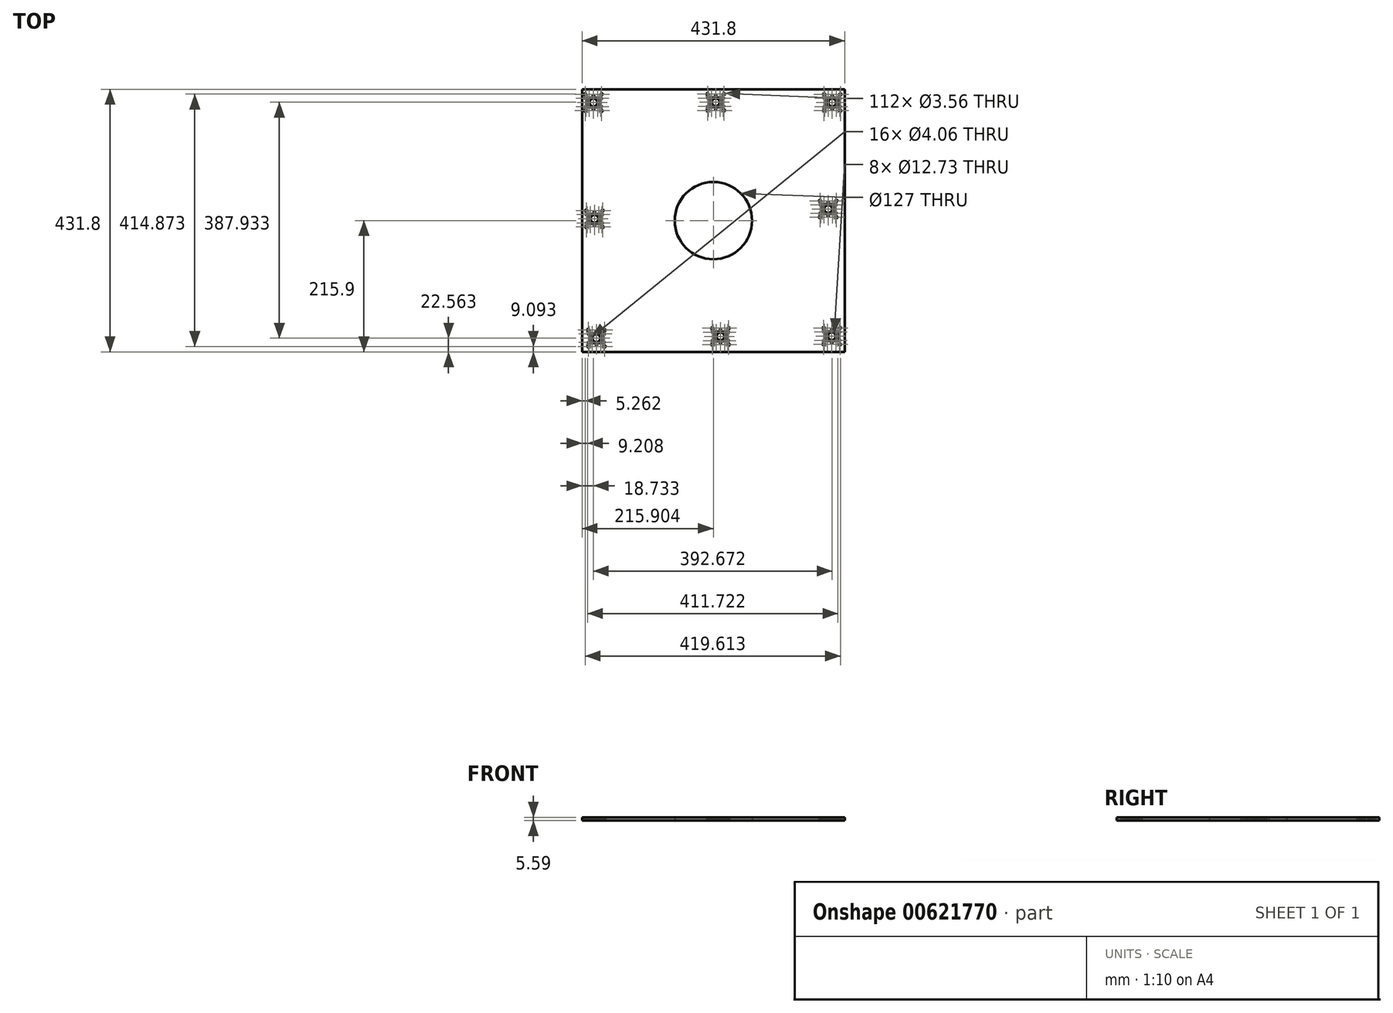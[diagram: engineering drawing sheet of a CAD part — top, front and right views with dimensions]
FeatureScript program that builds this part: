
annotation { "Feature Type Name" : "Feature", "Feature Type Description" : "" }
export const myFeature = defineFeature(function(context is Context, id is Id, definition is map)
    precondition{}
    {
        {
            var Q0;
            Q0=qCreatedBy(makeId("Top.planeOp"),FACE);
            var sketch = newSketch(context, id + "F0", { "sketchPlane" : qUnion([Q0])});
            skLineSegment(sketch, "E0.bottom", {"start": v(148.17, 142.22) * mm, "end": v(-283.63, 142.22) * mm});
            skLineSegment(sketch, "E0.top", {"start": v(148.17, -289.58) * mm, "end": v(-283.63, -289.58) * mm});
            skLineSegment(sketch, "E0.left", {"start": v(148.17, 142.22) * mm, "end": v(148.17, -289.58) * mm});
            skLineSegment(sketch, "E0.right", {"start": v(-283.63, 142.22) * mm, "end": v(-283.63, -289.58) * mm});
            skPoint(sketch, "E0.middle", {"position": v(-67.73, -73.68) * mm});
            skCircle(sketch, "E1", {"center": v(-264.9, 130.29) * mm, "radius": 1.78 * mm});
            skPoint(sketch, "E1.first.point", {"position": v(-264.85, 132.07) * mm});
            skPoint(sketch, "E1.second.point", {"position": v(-264.68, 128.52) * mm});
            skPoint(sketch, "E1.third.point", {"position": v(-266.67, 130.25) * mm});
            skCircle(sketch, "E2", {"center": v(-264.9, 110.73) * mm, "radius": 1.78 * mm});
            skPoint(sketch, "E2.first.point", {"position": v(-264.74, 108.96) * mm});
            skPoint(sketch, "E2.second.point", {"position": v(-263.7, 112.04) * mm});
            skPoint(sketch, "E2.third.point", {"position": v(-265.58, 112.37) * mm});
            skPoint(sketch, "E3.first.point", {"position": v(-271.06, 105.36) * mm});
            skPoint(sketch, "E3.second.point", {"position": v(-269.23, 108.3) * mm});
            skPoint(sketch, "E3.third.point", {"position": v(-272.02, 107.92) * mm});
            skPoint(sketch, "E4.first.point", {"position": v(-258.08, 105.76) * mm});
            skPoint(sketch, "E4.second.point", {"position": v(-259.26, 108.82) * mm});
            skPoint(sketch, "E4.third.point", {"position": v(-260.86, 106.16) * mm});
            skPoint(sketch, "E5.first.point", {"position": v(-259.07, 132.22) * mm});
            skPoint(sketch, "E5.second.point", {"position": v(-259.1, 135.74) * mm});
            skPoint(sketch, "E5.third.point", {"position": v(-261.06, 133.62) * mm});
            skPoint(sketch, "E6.first.point", {"position": v(-272.16, 133.4) * mm});
            skPoint(sketch, "E6.second.point", {"position": v(-269.17, 135.18) * mm});
            skPoint(sketch, "E6.third.point", {"position": v(-271.36, 135.52) * mm});
            skCircle(sketch, "E7", {"center": v(-278.37, 133.98) * mm, "radius": 1.78 * mm});
            skPoint(sketch, "E7.first.point", {"position": v(-278.3, 135.76) * mm});
            skPoint(sketch, "E7.second.point", {"position": v(-277.44, 132.47) * mm});
            skPoint(sketch, "E7.third.point", {"position": v(-279.88, 133.05) * mm});
            skCircle(sketch, "E8", {"center": v(-251.43, 133.98) * mm, "radius": 1.78 * mm});
            skPoint(sketch, "E8.first.point", {"position": v(-250.93, 132.27) * mm});
            skPoint(sketch, "E8.second.point", {"position": v(-251.22, 135.75) * mm});
            skPoint(sketch, "E8.third.point", {"position": v(-253.2, 133.75) * mm});
            skCircle(sketch, "E9", {"center": v(-252.76, 127.42) * mm, "radius": 1.78 * mm});
            skPoint(sketch, "E9.first.point", {"position": v(-252.48, 129.18) * mm});
            skPoint(sketch, "E9.second.point", {"position": v(-252.73, 125.65) * mm});
            skPoint(sketch, "E9.third.point", {"position": v(-253.73, 128.91) * mm});
            skCircle(sketch, "E10", {"center": v(-257.98, 127.42) * mm, "radius": 1.78 * mm});
            skPoint(sketch, "E10.first.point", {"position": v(-257.5, 125.71) * mm});
            skPoint(sketch, "E10.second.point", {"position": v(-257.84, 129.2) * mm});
            skPoint(sketch, "E10.third.point", {"position": v(-259.28, 128.64) * mm});
            skCircle(sketch, "E11", {"center": v(-271.81, 127.42) * mm, "radius": 1.78 * mm});
            skPoint(sketch, "E11.first.point", {"position": v(-272.14, 125.68) * mm});
            skPoint(sketch, "E11.second.point", {"position": v(-270.14, 128.03) * mm});
            skPoint(sketch, "E11.third.point", {"position": v(-272.1, 129.18) * mm});
            skCircle(sketch, "E12", {"center": v(-277.03, 127.42) * mm, "radius": 1.78 * mm});
            skPoint(sketch, "E12.first.point", {"position": v(-277, 125.65) * mm});
            skPoint(sketch, "E12.second.point", {"position": v(-276.26, 129.03) * mm});
            skPoint(sketch, "E12.third.point", {"position": v(-276.91, 129.2) * mm});
            skCircle(sketch, "E13", {"center": v(-274.42, 120.5) * mm, "radius": 2.03 * mm});
            skPoint(sketch, "E13.first.point", {"position": v(-273.06, 122.02) * mm});
            skPoint(sketch, "E13.second.point", {"position": v(-272.94, 119.12) * mm});
            skPoint(sketch, "E13.third.point", {"position": v(-276.18, 121.53) * mm});
            skCircle(sketch, "E14", {"center": v(-264.9, 120.5) * mm, "radius": 6.36 * mm});
            skPoint(sketch, "E14.first.point", {"position": v(-266.11, 114.26) * mm});
            skPoint(sketch, "E14.second.point", {"position": v(-259.17, 123.3) * mm});
            skPoint(sketch, "E14.third.point", {"position": v(-268.92, 125.44) * mm});
            skCircle(sketch, "E15", {"center": v(-255.37, 120.5) * mm, "radius": 2.03 * mm});
            skPoint(sketch, "E15.first.point", {"position": v(-255.23, 118.48) * mm});
            skPoint(sketch, "E15.second.point", {"position": v(-253.75, 121.73) * mm});
            skPoint(sketch, "E15.third.point", {"position": v(-255.78, 122.5) * mm});
            skCircle(sketch, "E16", {"center": v(-252.76, 113.6) * mm, "radius": 1.78 * mm});
            skPoint(sketch, "E16.first.point", {"position": v(-252.64, 111.82) * mm});
            skPoint(sketch, "E16.second.point", {"position": v(-251.22, 114.48) * mm});
            skPoint(sketch, "E16.third.point", {"position": v(-253.96, 114.91) * mm});
            skCircle(sketch, "E17", {"center": v(-257.98, 113.6) * mm, "radius": 1.78 * mm});
            skPoint(sketch, "E17.first.point", {"position": v(-258.1, 111.82) * mm});
            skPoint(sketch, "E17.second.point", {"position": v(-257.07, 115.12) * mm});
            skPoint(sketch, "E17.third.point", {"position": v(-258.86, 115.14) * mm});
            skCircle(sketch, "E18", {"center": v(-251.43, 107.04) * mm, "radius": 1.78 * mm});
            skPoint(sketch, "E18.first.point", {"position": v(-252.64, 105.74) * mm});
            skPoint(sketch, "E18.second.point", {"position": v(-250.38, 108.48) * mm});
            skPoint(sketch, "E18.third.point", {"position": v(-250.31, 105.65) * mm});
            skCircle(sketch, "E19", {"center": v(-278.37, 107.04) * mm, "radius": 1.78 * mm});
            skPoint(sketch, "E19.first.point", {"position": v(-278.95, 105.36) * mm});
            skPoint(sketch, "E19.second.point", {"position": v(-276.98, 108.16) * mm});
            skPoint(sketch, "E19.third.point", {"position": v(-279.64, 108.28) * mm});
            skCircle(sketch, "E20", {"center": v(-277.03, 113.6) * mm, "radius": 1.78 * mm});
            skPoint(sketch, "E20.first.point", {"position": v(-277.43, 111.86) * mm});
            skPoint(sketch, "E20.second.point", {"position": v(-275.8, 114.88) * mm});
            skPoint(sketch, "E20.third.point", {"position": v(-277.51, 115.3) * mm});
            skCircle(sketch, "E21", {"center": v(-271.81, 113.6) * mm, "radius": 1.78 * mm});
            skPoint(sketch, "E21.first.point", {"position": v(-272.24, 111.87) * mm});
            skPoint(sketch, "E21.second.point", {"position": v(-271.06, 115.2) * mm});
            skPoint(sketch, "E21.third.point", {"position": v(-272.97, 114.94) * mm});
            skCircle(sketch, "E22", {"center": v(127.77, 130.29) * mm, "radius": 1.78 * mm});
            skPoint(sketch, "E22.first.point", {"position": v(127.83, 132.07) * mm});
            skPoint(sketch, "E22.second.point", {"position": v(128, 128.52) * mm});
            skPoint(sketch, "E22.third.point", {"position": v(126, 130.25) * mm});
            skCircle(sketch, "E23", {"center": v(127.77, 110.73) * mm, "radius": 1.78 * mm});
            skPoint(sketch, "E23.first.point", {"position": v(127.93, 108.96) * mm});
            skPoint(sketch, "E23.second.point", {"position": v(128.98, 112.04) * mm});
            skPoint(sketch, "E23.third.point", {"position": v(127.1, 112.37) * mm});
            skPoint(sketch, "E24.first.point", {"position": v(121.62, 105.36) * mm});
            skPoint(sketch, "E24.second.point", {"position": v(123.44, 108.3) * mm});
            skPoint(sketch, "E24.third.point", {"position": v(120.65, 107.92) * mm});
            skPoint(sketch, "E25.first.point", {"position": v(134.6, 105.76) * mm});
            skPoint(sketch, "E25.second.point", {"position": v(133.41, 108.82) * mm});
            skPoint(sketch, "E25.third.point", {"position": v(131.81, 106.16) * mm});
            skPoint(sketch, "E26.first.point", {"position": v(133.6, 132.22) * mm});
            skPoint(sketch, "E26.second.point", {"position": v(133.57, 135.74) * mm});
            skPoint(sketch, "E26.third.point", {"position": v(131.61, 133.62) * mm});
            skPoint(sketch, "E27.first.point", {"position": v(120.51, 133.4) * mm});
            skPoint(sketch, "E27.second.point", {"position": v(123.5, 135.18) * mm});
            skPoint(sketch, "E27.third.point", {"position": v(121.31, 135.52) * mm});
            skCircle(sketch, "E28", {"center": v(114.3, 133.98) * mm, "radius": 1.78 * mm});
            skPoint(sketch, "E28.first.point", {"position": v(114.38, 135.76) * mm});
            skPoint(sketch, "E28.second.point", {"position": v(115.24, 132.47) * mm});
            skPoint(sketch, "E28.third.point", {"position": v(112.8, 133.05) * mm});
            skCircle(sketch, "E29", {"center": v(141.25, 133.98) * mm, "radius": 1.78 * mm});
            skPoint(sketch, "E29.first.point", {"position": v(141.74, 132.27) * mm});
            skPoint(sketch, "E29.second.point", {"position": v(141.45, 135.75) * mm});
            skPoint(sketch, "E29.third.point", {"position": v(139.48, 133.75) * mm});
            skCircle(sketch, "E30", {"center": v(139.91, 127.42) * mm, "radius": 1.78 * mm});
            skPoint(sketch, "E30.first.point", {"position": v(140.2, 129.18) * mm});
            skPoint(sketch, "E30.second.point", {"position": v(139.94, 125.65) * mm});
            skPoint(sketch, "E30.third.point", {"position": v(138.94, 128.91) * mm});
            skCircle(sketch, "E31", {"center": v(134.69, 127.42) * mm, "radius": 1.78 * mm});
            skPoint(sketch, "E31.first.point", {"position": v(135.18, 125.71) * mm});
            skPoint(sketch, "E31.second.point", {"position": v(134.83, 129.2) * mm});
            skPoint(sketch, "E31.third.point", {"position": v(133.4, 128.64) * mm});
            skCircle(sketch, "E32", {"center": v(120.86, 127.42) * mm, "radius": 1.78 * mm});
            skPoint(sketch, "E32.first.point", {"position": v(120.54, 125.68) * mm});
            skPoint(sketch, "E32.second.point", {"position": v(122.53, 128.03) * mm});
            skPoint(sketch, "E32.third.point", {"position": v(120.58, 129.18) * mm});
            skCircle(sketch, "E33", {"center": v(115.64, 127.42) * mm, "radius": 1.78 * mm});
            skPoint(sketch, "E33.first.point", {"position": v(115.67, 125.65) * mm});
            skPoint(sketch, "E33.second.point", {"position": v(116.41, 129.03) * mm});
            skPoint(sketch, "E33.third.point", {"position": v(115.76, 129.2) * mm});
            skCircle(sketch, "E34", {"center": v(118.25, 120.5) * mm, "radius": 2.03 * mm});
            skPoint(sketch, "E34.first.point", {"position": v(119.61, 122.02) * mm});
            skPoint(sketch, "E34.second.point", {"position": v(119.74, 119.12) * mm});
            skPoint(sketch, "E34.third.point", {"position": v(116.5, 121.53) * mm});
            skCircle(sketch, "E35", {"center": v(127.77, 120.5) * mm, "radius": 6.36 * mm});
            skPoint(sketch, "E35.first.point", {"position": v(126.56, 114.26) * mm});
            skPoint(sketch, "E35.second.point", {"position": v(133.5, 123.3) * mm});
            skPoint(sketch, "E35.third.point", {"position": v(123.75, 125.44) * mm});
            skCircle(sketch, "E36", {"center": v(137.3, 120.5) * mm, "radius": 2.03 * mm});
            skPoint(sketch, "E36.first.point", {"position": v(137.44, 118.48) * mm});
            skPoint(sketch, "E36.second.point", {"position": v(138.93, 121.73) * mm});
            skPoint(sketch, "E36.third.point", {"position": v(136.9, 122.5) * mm});
            skCircle(sketch, "E37", {"center": v(139.91, 113.6) * mm, "radius": 1.78 * mm});
            skPoint(sketch, "E37.first.point", {"position": v(140.03, 111.82) * mm});
            skPoint(sketch, "E37.second.point", {"position": v(141.45, 114.48) * mm});
            skPoint(sketch, "E37.third.point", {"position": v(138.72, 114.91) * mm});
            skCircle(sketch, "E38", {"center": v(134.69, 113.6) * mm, "radius": 1.78 * mm});
            skPoint(sketch, "E38.first.point", {"position": v(134.58, 111.82) * mm});
            skPoint(sketch, "E38.second.point", {"position": v(135.6, 115.12) * mm});
            skPoint(sketch, "E38.third.point", {"position": v(133.81, 115.14) * mm});
            skCircle(sketch, "E39", {"center": v(141.25, 107.04) * mm, "radius": 1.78 * mm});
            skPoint(sketch, "E39.first.point", {"position": v(140.03, 105.74) * mm});
            skPoint(sketch, "E39.second.point", {"position": v(142.3, 108.48) * mm});
            skPoint(sketch, "E39.third.point", {"position": v(142.36, 105.65) * mm});
            skCircle(sketch, "E40", {"center": v(114.3, 107.04) * mm, "radius": 1.78 * mm});
            skPoint(sketch, "E40.first.point", {"position": v(113.73, 105.36) * mm});
            skPoint(sketch, "E40.second.point", {"position": v(115.69, 108.16) * mm});
            skPoint(sketch, "E40.third.point", {"position": v(113.03, 108.28) * mm});
            skCircle(sketch, "E41", {"center": v(115.64, 113.6) * mm, "radius": 1.78 * mm});
            skPoint(sketch, "E41.first.point", {"position": v(115.24, 111.86) * mm});
            skPoint(sketch, "E41.second.point", {"position": v(116.87, 114.88) * mm});
            skPoint(sketch, "E41.third.point", {"position": v(115.16, 115.3) * mm});
            skCircle(sketch, "E42", {"center": v(120.86, 113.6) * mm, "radius": 1.78 * mm});
            skPoint(sketch, "E42.first.point", {"position": v(120.43, 111.87) * mm});
            skPoint(sketch, "E42.second.point", {"position": v(121.62, 115.2) * mm});
            skPoint(sketch, "E42.third.point", {"position": v(119.7, 114.94) * mm});
            skCircle(sketch, "E43", {"center": v(-63.84, 130.7) * mm, "radius": 1.78 * mm});
            skPoint(sketch, "E43.first.point", {"position": v(-63.78, 132.47) * mm});
            skPoint(sketch, "E43.second.point", {"position": v(-63.62, 128.93) * mm});
            skPoint(sketch, "E43.third.point", {"position": v(-65.61, 130.66) * mm});
            skCircle(sketch, "E44", {"center": v(-63.84, 111.14) * mm, "radius": 1.78 * mm});
            skPoint(sketch, "E44.first.point", {"position": v(-63.68, 109.37) * mm});
            skPoint(sketch, "E44.second.point", {"position": v(-62.63, 112.44) * mm});
            skPoint(sketch, "E44.third.point", {"position": v(-64.52, 112.78) * mm});
            skPoint(sketch, "E45.first.point", {"position": v(-70, 105.76) * mm});
            skPoint(sketch, "E45.second.point", {"position": v(-68.17, 108.71) * mm});
            skPoint(sketch, "E45.third.point", {"position": v(-70.96, 108.32) * mm});
            skPoint(sketch, "E46.first.point", {"position": v(-57.02, 106.17) * mm});
            skPoint(sketch, "E46.second.point", {"position": v(-58.2, 109.22) * mm});
            skPoint(sketch, "E46.third.point", {"position": v(-59.8, 106.56) * mm});
            skPoint(sketch, "E47.first.point", {"position": v(-58, 132.63) * mm});
            skPoint(sketch, "E47.second.point", {"position": v(-58.04, 136.15) * mm});
            skPoint(sketch, "E47.third.point", {"position": v(-60, 134.03) * mm});
            skPoint(sketch, "E48.first.point", {"position": v(-71.1, 133.8) * mm});
            skPoint(sketch, "E48.second.point", {"position": v(-68.1, 135.6) * mm});
            skPoint(sketch, "E48.third.point", {"position": v(-70.3, 135.93) * mm});
            skCircle(sketch, "E49", {"center": v(-77.3, 134.39) * mm, "radius": 1.78 * mm});
            skPoint(sketch, "E49.first.point", {"position": v(-77.23, 136.16) * mm});
            skPoint(sketch, "E49.second.point", {"position": v(-76.38, 132.87) * mm});
            skPoint(sketch, "E49.third.point", {"position": v(-78.82, 133.45) * mm});
            skCircle(sketch, "E50", {"center": v(-50.37, 134.39) * mm, "radius": 1.78 * mm});
            skPoint(sketch, "E50.first.point", {"position": v(-49.87, 132.68) * mm});
            skPoint(sketch, "E50.second.point", {"position": v(-50.16, 136.15) * mm});
            skPoint(sketch, "E50.third.point", {"position": v(-52.13, 134.16) * mm});
            skCircle(sketch, "E51", {"center": v(-51.7, 127.83) * mm, "radius": 1.78 * mm});
            skPoint(sketch, "E51.first.point", {"position": v(-51.42, 129.59) * mm});
            skPoint(sketch, "E51.second.point", {"position": v(-51.67, 126.05) * mm});
            skPoint(sketch, "E51.third.point", {"position": v(-52.67, 129.32) * mm});
            skCircle(sketch, "E52", {"center": v(-56.92, 127.83) * mm, "radius": 1.78 * mm});
            skPoint(sketch, "E52.first.point", {"position": v(-56.43, 126.12) * mm});
            skPoint(sketch, "E52.second.point", {"position": v(-56.78, 129.6) * mm});
            skPoint(sketch, "E52.third.point", {"position": v(-58.21, 129.05) * mm});
            skCircle(sketch, "E53", {"center": v(-70.75, 127.83) * mm, "radius": 1.78 * mm});
            skPoint(sketch, "E53.first.point", {"position": v(-71.08, 126.08) * mm});
            skPoint(sketch, "E53.second.point", {"position": v(-69.08, 128.43) * mm});
            skPoint(sketch, "E53.third.point", {"position": v(-71.03, 129.59) * mm});
            skCircle(sketch, "E54", {"center": v(-75.97, 127.83) * mm, "radius": 1.78 * mm});
            skPoint(sketch, "E54.first.point", {"position": v(-75.94, 126.05) * mm});
            skPoint(sketch, "E54.second.point", {"position": v(-75.2, 129.43) * mm});
            skPoint(sketch, "E54.third.point", {"position": v(-75.85, 129.6) * mm});
            skCircle(sketch, "E55", {"center": v(-73.36, 120.92) * mm, "radius": 2.03 * mm});
            skPoint(sketch, "E55.first.point", {"position": v(-72, 122.43) * mm});
            skPoint(sketch, "E55.second.point", {"position": v(-71.88, 119.53) * mm});
            skPoint(sketch, "E55.third.point", {"position": v(-75.12, 121.94) * mm});
            skCircle(sketch, "E56", {"center": v(-63.84, 120.92) * mm, "radius": 6.36 * mm});
            skPoint(sketch, "E56.first.point", {"position": v(-65.05, 114.67) * mm});
            skPoint(sketch, "E56.second.point", {"position": v(-58.11, 123.7) * mm});
            skPoint(sketch, "E56.third.point", {"position": v(-67.86, 125.85) * mm});
            skCircle(sketch, "E57", {"center": v(-54.31, 120.92) * mm, "radius": 2.03 * mm});
            skPoint(sketch, "E57.first.point", {"position": v(-54.17, 118.89) * mm});
            skPoint(sketch, "E57.second.point", {"position": v(-52.69, 122.13) * mm});
            skPoint(sketch, "E57.third.point", {"position": v(-54.72, 122.9) * mm});
            skCircle(sketch, "E58", {"center": v(-51.7, 114) * mm, "radius": 1.78 * mm});
            skPoint(sketch, "E58.first.point", {"position": v(-51.58, 112.23) * mm});
            skPoint(sketch, "E58.second.point", {"position": v(-50.16, 114.88) * mm});
            skPoint(sketch, "E58.third.point", {"position": v(-52.9, 115.32) * mm});
            skCircle(sketch, "E59", {"center": v(-56.92, 114) * mm, "radius": 1.78 * mm});
            skPoint(sketch, "E59.first.point", {"position": v(-57.03, 112.23) * mm});
            skPoint(sketch, "E59.second.point", {"position": v(-56.01, 115.53) * mm});
            skPoint(sketch, "E59.third.point", {"position": v(-57.8, 115.55) * mm});
            skCircle(sketch, "E60", {"center": v(-50.37, 107.45) * mm, "radius": 1.78 * mm});
            skPoint(sketch, "E60.first.point", {"position": v(-51.58, 106.14) * mm});
            skPoint(sketch, "E60.second.point", {"position": v(-49.32, 108.88) * mm});
            skPoint(sketch, "E60.third.point", {"position": v(-49.25, 106.06) * mm});
            skCircle(sketch, "E61", {"center": v(-77.3, 107.45) * mm, "radius": 1.78 * mm});
            skPoint(sketch, "E61.first.point", {"position": v(-77.89, 105.76) * mm});
            skPoint(sketch, "E61.second.point", {"position": v(-75.92, 108.56) * mm});
            skPoint(sketch, "E61.third.point", {"position": v(-78.58, 108.68) * mm});
            skCircle(sketch, "E62", {"center": v(-75.97, 114) * mm, "radius": 1.78 * mm});
            skPoint(sketch, "E62.first.point", {"position": v(-76.37, 112.27) * mm});
            skPoint(sketch, "E62.second.point", {"position": v(-74.74, 115.29) * mm});
            skPoint(sketch, "E62.third.point", {"position": v(-76.45, 115.71) * mm});
            skCircle(sketch, "E63", {"center": v(-70.75, 114) * mm, "radius": 1.78 * mm});
            skPoint(sketch, "E63.first.point", {"position": v(-71.18, 112.27) * mm});
            skPoint(sketch, "E63.second.point", {"position": v(-70, 115.6) * mm});
            skPoint(sketch, "E63.third.point", {"position": v(-71.9, 115.35) * mm});
            skCircle(sketch, "E64", {"center": v(-263.17, -60.9) * mm, "radius": 1.78 * mm});
            skPoint(sketch, "E64.first.point", {"position": v(-263.11, -59.11) * mm});
            skPoint(sketch, "E64.second.point", {"position": v(-262.95, -62.66) * mm});
            skPoint(sketch, "E64.third.point", {"position": v(-264.94, -60.93) * mm});
            skCircle(sketch, "E65", {"center": v(-263.17, -80.45) * mm, "radius": 1.78 * mm});
            skPoint(sketch, "E65.first.point", {"position": v(-263, -82.22) * mm});
            skPoint(sketch, "E65.second.point", {"position": v(-261.96, -79.14) * mm});
            skPoint(sketch, "E65.third.point", {"position": v(-263.85, -78.8) * mm});
            skPoint(sketch, "E66.first.point", {"position": v(-269.33, -85.82) * mm});
            skPoint(sketch, "E66.second.point", {"position": v(-267.5, -82.87) * mm});
            skPoint(sketch, "E66.third.point", {"position": v(-270.3, -83.26) * mm});
            skPoint(sketch, "E67.first.point", {"position": v(-256.35, -85.42) * mm});
            skPoint(sketch, "E67.second.point", {"position": v(-257.53, -82.36) * mm});
            skPoint(sketch, "E67.third.point", {"position": v(-259.13, -85.02) * mm});
            skPoint(sketch, "E68.first.point", {"position": v(-257.34, -58.96) * mm});
            skPoint(sketch, "E68.second.point", {"position": v(-257.37, -55.44) * mm});
            skPoint(sketch, "E68.third.point", {"position": v(-259.33, -57.56) * mm});
            skPoint(sketch, "E69.first.point", {"position": v(-270.43, -57.78) * mm});
            skPoint(sketch, "E69.second.point", {"position": v(-267.44, -56) * mm});
            skPoint(sketch, "E69.third.point", {"position": v(-269.63, -55.66) * mm});
            skCircle(sketch, "E70", {"center": v(-276.64, -57.2) * mm, "radius": 1.78 * mm});
            skPoint(sketch, "E70.first.point", {"position": v(-276.56, -55.42) * mm});
            skPoint(sketch, "E70.second.point", {"position": v(-275.7, -58.71) * mm});
            skPoint(sketch, "E70.third.point", {"position": v(-278.15, -58.13) * mm});
            skCircle(sketch, "E71", {"center": v(-249.7, -57.2) * mm, "radius": 1.78 * mm});
            skPoint(sketch, "E71.first.point", {"position": v(-249.2, -58.9) * mm});
            skPoint(sketch, "E71.second.point", {"position": v(-249.5, -55.43) * mm});
            skPoint(sketch, "E71.third.point", {"position": v(-251.46, -57.43) * mm});
            skCircle(sketch, "E72", {"center": v(-251.03, -63.76) * mm, "radius": 1.78 * mm});
            skPoint(sketch, "E72.first.point", {"position": v(-250.75, -62) * mm});
            skPoint(sketch, "E72.second.point", {"position": v(-251, -65.53) * mm});
            skPoint(sketch, "E72.third.point", {"position": v(-252, -62.27) * mm});
            skCircle(sketch, "E73", {"center": v(-256.25, -63.76) * mm, "radius": 1.78 * mm});
            skPoint(sketch, "E73.first.point", {"position": v(-255.76, -65.47) * mm});
            skPoint(sketch, "E73.second.point", {"position": v(-256.11, -61.98) * mm});
            skPoint(sketch, "E73.third.point", {"position": v(-257.54, -62.53) * mm});
            skCircle(sketch, "E74", {"center": v(-270.08, -63.76) * mm, "radius": 1.78 * mm});
            skPoint(sketch, "E74.first.point", {"position": v(-270.4, -65.5) * mm});
            skPoint(sketch, "E74.second.point", {"position": v(-268.4, -63.15) * mm});
            skPoint(sketch, "E74.third.point", {"position": v(-270.36, -62) * mm});
            skCircle(sketch, "E75", {"center": v(-275.3, -63.76) * mm, "radius": 1.78 * mm});
            skPoint(sketch, "E75.first.point", {"position": v(-275.27, -65.53) * mm});
            skPoint(sketch, "E75.second.point", {"position": v(-274.53, -62.15) * mm});
            skPoint(sketch, "E75.third.point", {"position": v(-275.18, -61.98) * mm});
            skCircle(sketch, "E76", {"center": v(-272.7, -70.67) * mm, "radius": 2.03 * mm});
            skPoint(sketch, "E76.first.point", {"position": v(-271.33, -69.16) * mm});
            skPoint(sketch, "E76.second.point", {"position": v(-271.2, -72.06) * mm});
            skPoint(sketch, "E76.third.point", {"position": v(-274.45, -69.65) * mm});
            skCircle(sketch, "E77", {"center": v(-263.17, -70.67) * mm, "radius": 6.36 * mm});
            skPoint(sketch, "E77.first.point", {"position": v(-264.38, -76.92) * mm});
            skPoint(sketch, "E77.second.point", {"position": v(-257.44, -67.89) * mm});
            skPoint(sketch, "E77.third.point", {"position": v(-267.19, -65.74) * mm});
            skCircle(sketch, "E78", {"center": v(-253.64, -70.67) * mm, "radius": 2.03 * mm});
            skPoint(sketch, "E78.first.point", {"position": v(-253.5, -72.7) * mm});
            skPoint(sketch, "E78.second.point", {"position": v(-252.02, -69.45) * mm});
            skPoint(sketch, "E78.third.point", {"position": v(-254.05, -68.68) * mm});
            skCircle(sketch, "E79", {"center": v(-251.03, -77.58) * mm, "radius": 1.78 * mm});
            skPoint(sketch, "E79.first.point", {"position": v(-250.9, -79.36) * mm});
            skPoint(sketch, "E79.second.point", {"position": v(-249.49, -76.7) * mm});
            skPoint(sketch, "E79.third.point", {"position": v(-252.22, -76.27) * mm});
            skCircle(sketch, "E80", {"center": v(-256.25, -77.58) * mm, "radius": 1.78 * mm});
            skPoint(sketch, "E80.first.point", {"position": v(-256.36, -79.36) * mm});
            skPoint(sketch, "E80.second.point", {"position": v(-255.34, -76.06) * mm});
            skPoint(sketch, "E80.third.point", {"position": v(-257.13, -76.04) * mm});
            skCircle(sketch, "E81", {"center": v(-249.7, -84.14) * mm, "radius": 1.78 * mm});
            skPoint(sketch, "E81.first.point", {"position": v(-250.9, -85.44) * mm});
            skPoint(sketch, "E81.second.point", {"position": v(-248.65, -82.7) * mm});
            skPoint(sketch, "E81.third.point", {"position": v(-248.58, -85.53) * mm});
            skCircle(sketch, "E82", {"center": v(-276.64, -84.14) * mm, "radius": 1.78 * mm});
            skPoint(sketch, "E82.first.point", {"position": v(-277.22, -85.82) * mm});
            skPoint(sketch, "E82.second.point", {"position": v(-275.25, -83.02) * mm});
            skPoint(sketch, "E82.third.point", {"position": v(-277.91, -82.9) * mm});
            skCircle(sketch, "E83", {"center": v(-275.3, -77.58) * mm, "radius": 1.78 * mm});
            skPoint(sketch, "E83.first.point", {"position": v(-275.7, -79.32) * mm});
            skPoint(sketch, "E83.second.point", {"position": v(-274.07, -76.3) * mm});
            skPoint(sketch, "E83.third.point", {"position": v(-275.78, -75.87) * mm});
            skCircle(sketch, "E84", {"center": v(-270.08, -77.58) * mm, "radius": 1.78 * mm});
            skPoint(sketch, "E84.first.point", {"position": v(-270.5, -79.31) * mm});
            skPoint(sketch, "E84.second.point", {"position": v(-269.33, -75.98) * mm});
            skPoint(sketch, "E84.third.point", {"position": v(-271.24, -76.24) * mm});
            skCircle(sketch, "E85", {"center": v(-260.03, -257.24) * mm, "radius": 1.78 * mm});
            skPoint(sketch, "E85.first.point", {"position": v(-259.97, -255.46) * mm});
            skPoint(sketch, "E85.second.point", {"position": v(-259.8, -259) * mm});
            skPoint(sketch, "E85.third.point", {"position": v(-261.8, -257.28) * mm});
            skCircle(sketch, "E86", {"center": v(-260.03, -276.8) * mm, "radius": 1.78 * mm});
            skPoint(sketch, "E86.first.point", {"position": v(-259.87, -278.57) * mm});
            skPoint(sketch, "E86.second.point", {"position": v(-258.82, -275.49) * mm});
            skPoint(sketch, "E86.third.point", {"position": v(-260.7, -275.15) * mm});
            skPoint(sketch, "E87.first.point", {"position": v(-266.18, -282.17) * mm});
            skPoint(sketch, "E87.second.point", {"position": v(-264.36, -279.22) * mm});
            skPoint(sketch, "E87.third.point", {"position": v(-267.15, -279.6) * mm});
            skPoint(sketch, "E88.first.point", {"position": v(-253.2, -281.76) * mm});
            skPoint(sketch, "E88.second.point", {"position": v(-254.39, -278.71) * mm});
            skPoint(sketch, "E88.third.point", {"position": v(-255.99, -281.37) * mm});
            skPoint(sketch, "E89.first.point", {"position": v(-254.2, -255.3) * mm});
            skPoint(sketch, "E89.second.point", {"position": v(-254.23, -251.78) * mm});
            skPoint(sketch, "E89.third.point", {"position": v(-256.19, -253.9) * mm});
            skPoint(sketch, "E90.first.point", {"position": v(-267.29, -254.13) * mm});
            skPoint(sketch, "E90.second.point", {"position": v(-264.3, -252.34) * mm});
            skPoint(sketch, "E90.third.point", {"position": v(-266.49, -252) * mm});
            skCircle(sketch, "E91", {"center": v(-273.5, -253.55) * mm, "radius": 1.78 * mm});
            skPoint(sketch, "E91.first.point", {"position": v(-273.42, -251.77) * mm});
            skPoint(sketch, "E91.second.point", {"position": v(-272.56, -255.06) * mm});
            skPoint(sketch, "E91.third.point", {"position": v(-275, -254.48) * mm});
            skCircle(sketch, "E92", {"center": v(-246.55, -253.55) * mm, "radius": 1.78 * mm});
            skPoint(sketch, "E92.first.point", {"position": v(-246.06, -255.25) * mm});
            skPoint(sketch, "E92.second.point", {"position": v(-246.35, -251.78) * mm});
            skPoint(sketch, "E92.third.point", {"position": v(-248.32, -253.77) * mm});
            skCircle(sketch, "E93", {"center": v(-247.89, -260.1) * mm, "radius": 1.78 * mm});
            skPoint(sketch, "E93.first.point", {"position": v(-247.6, -258.35) * mm});
            skPoint(sketch, "E93.second.point", {"position": v(-247.86, -261.88) * mm});
            skPoint(sketch, "E93.third.point", {"position": v(-248.86, -258.61) * mm});
            skCircle(sketch, "E94", {"center": v(-253.11, -260.1) * mm, "radius": 1.78 * mm});
            skPoint(sketch, "E94.first.point", {"position": v(-252.62, -261.81) * mm});
            skPoint(sketch, "E94.second.point", {"position": v(-252.97, -258.33) * mm});
            skPoint(sketch, "E94.third.point", {"position": v(-254.4, -258.88) * mm});
            skCircle(sketch, "E95", {"center": v(-266.94, -260.1) * mm, "radius": 1.78 * mm});
            skPoint(sketch, "E95.first.point", {"position": v(-267.26, -261.85) * mm});
            skPoint(sketch, "E95.second.point", {"position": v(-265.27, -259.5) * mm});
            skPoint(sketch, "E95.third.point", {"position": v(-267.22, -258.35) * mm});
            skCircle(sketch, "E96", {"center": v(-272.16, -260.1) * mm, "radius": 1.78 * mm});
            skPoint(sketch, "E96.first.point", {"position": v(-272.13, -261.88) * mm});
            skPoint(sketch, "E96.second.point", {"position": v(-271.39, -258.5) * mm});
            skPoint(sketch, "E96.third.point", {"position": v(-272.04, -258.33) * mm});
            skCircle(sketch, "E97", {"center": v(-269.55, -267.02) * mm, "radius": 2.03 * mm});
            skPoint(sketch, "E97.first.point", {"position": v(-268.19, -265.5) * mm});
            skPoint(sketch, "E97.second.point", {"position": v(-268.06, -268.4) * mm});
            skPoint(sketch, "E97.third.point", {"position": v(-271.3, -266) * mm});
            skCircle(sketch, "E98", {"center": v(-260.03, -267.02) * mm, "radius": 6.36 * mm});
            skPoint(sketch, "E98.first.point", {"position": v(-261.24, -273.26) * mm});
            skPoint(sketch, "E98.second.point", {"position": v(-254.3, -264.24) * mm});
            skPoint(sketch, "E98.third.point", {"position": v(-264.05, -262.09) * mm});
            skCircle(sketch, "E99", {"center": v(-250.5, -267.02) * mm, "radius": 2.03 * mm});
            skPoint(sketch, "E99.first.point", {"position": v(-250.36, -269.04) * mm});
            skPoint(sketch, "E99.second.point", {"position": v(-248.87, -265.8) * mm});
            skPoint(sketch, "E99.third.point", {"position": v(-250.9, -265.03) * mm});
            skCircle(sketch, "E100", {"center": v(-247.89, -273.93) * mm, "radius": 1.78 * mm});
            skPoint(sketch, "E100.first.point", {"position": v(-247.77, -275.7) * mm});
            skPoint(sketch, "E100.second.point", {"position": v(-246.35, -273.05) * mm});
            skPoint(sketch, "E100.third.point", {"position": v(-249.08, -272.61) * mm});
            skCircle(sketch, "E101", {"center": v(-253.11, -273.93) * mm, "radius": 1.78 * mm});
            skPoint(sketch, "E101.first.point", {"position": v(-253.22, -275.7) * mm});
            skPoint(sketch, "E101.second.point", {"position": v(-252.2, -272.4) * mm});
            skPoint(sketch, "E101.third.point", {"position": v(-253.99, -272.39) * mm});
            skCircle(sketch, "E102", {"center": v(-246.55, -280.49) * mm, "radius": 1.78 * mm});
            skPoint(sketch, "E102.first.point", {"position": v(-247.77, -281.79) * mm});
            skPoint(sketch, "E102.second.point", {"position": v(-245.5, -279.05) * mm});
            skPoint(sketch, "E102.third.point", {"position": v(-245.44, -281.87) * mm});
            skCircle(sketch, "E103", {"center": v(-273.5, -280.49) * mm, "radius": 1.78 * mm});
            skPoint(sketch, "E103.first.point", {"position": v(-274.07, -282.17) * mm});
            skPoint(sketch, "E103.second.point", {"position": v(-272.11, -279.37) * mm});
            skPoint(sketch, "E103.third.point", {"position": v(-274.77, -279.25) * mm});
            skCircle(sketch, "E104", {"center": v(-272.16, -273.93) * mm, "radius": 1.78 * mm});
            skPoint(sketch, "E104.first.point", {"position": v(-272.56, -275.66) * mm});
            skPoint(sketch, "E104.second.point", {"position": v(-270.93, -272.65) * mm});
            skPoint(sketch, "E104.third.point", {"position": v(-272.64, -272.22) * mm});
            skCircle(sketch, "E105", {"center": v(-266.94, -273.93) * mm, "radius": 1.78 * mm});
            skPoint(sketch, "E105.first.point", {"position": v(-267.37, -275.66) * mm});
            skPoint(sketch, "E105.second.point", {"position": v(-266.18, -272.32) * mm});
            skPoint(sketch, "E105.third.point", {"position": v(-268.1, -272.58) * mm});
            skCircle(sketch, "E106", {"center": v(-55.95, -254.29) * mm, "radius": 1.78 * mm});
            skPoint(sketch, "E106.first.point", {"position": v(-55.9, -252.51) * mm});
            skPoint(sketch, "E106.second.point", {"position": v(-55.72, -256.05) * mm});
            skPoint(sketch, "E106.third.point", {"position": v(-57.72, -254.33) * mm});
            skCircle(sketch, "E107", {"center": v(-55.95, -273.85) * mm, "radius": 1.78 * mm});
            skPoint(sketch, "E107.first.point", {"position": v(-55.79, -275.62) * mm});
            skPoint(sketch, "E107.second.point", {"position": v(-54.74, -272.54) * mm});
            skPoint(sketch, "E107.third.point", {"position": v(-56.63, -272.2) * mm});
            skPoint(sketch, "E108.first.point", {"position": v(-62.1, -279.22) * mm});
            skPoint(sketch, "E108.second.point", {"position": v(-60.28, -276.27) * mm});
            skPoint(sketch, "E108.third.point", {"position": v(-63.07, -276.66) * mm});
            skPoint(sketch, "E109.first.point", {"position": v(-49.13, -278.81) * mm});
            skPoint(sketch, "E109.second.point", {"position": v(-50.3, -275.76) * mm});
            skPoint(sketch, "E109.third.point", {"position": v(-51.9, -278.42) * mm});
            skPoint(sketch, "E110.first.point", {"position": v(-50.11, -252.36) * mm});
            skPoint(sketch, "E110.second.point", {"position": v(-50.15, -248.83) * mm});
            skPoint(sketch, "E110.third.point", {"position": v(-52.1, -250.96) * mm});
            skPoint(sketch, "E111.first.point", {"position": v(-63.2, -251.18) * mm});
            skPoint(sketch, "E111.second.point", {"position": v(-60.22, -249.4) * mm});
            skPoint(sketch, "E111.third.point", {"position": v(-62.4, -249.05) * mm});
            skCircle(sketch, "E112", {"center": v(-69.42, -250.6) * mm, "radius": 1.78 * mm});
            skPoint(sketch, "E112.first.point", {"position": v(-69.34, -248.82) * mm});
            skPoint(sketch, "E112.second.point", {"position": v(-68.49, -252.11) * mm});
            skPoint(sketch, "E112.third.point", {"position": v(-70.93, -251.53) * mm});
            skCircle(sketch, "E113", {"center": v(-42.48, -250.6) * mm, "radius": 1.78 * mm});
            skPoint(sketch, "E113.first.point", {"position": v(-41.98, -252.3) * mm});
            skPoint(sketch, "E113.second.point", {"position": v(-42.27, -248.83) * mm});
            skPoint(sketch, "E113.third.point", {"position": v(-44.24, -250.82) * mm});
            skCircle(sketch, "E114", {"center": v(-43.81, -257.15) * mm, "radius": 1.78 * mm});
            skPoint(sketch, "E114.first.point", {"position": v(-43.53, -255.4) * mm});
            skPoint(sketch, "E114.second.point", {"position": v(-43.78, -258.93) * mm});
            skPoint(sketch, "E114.third.point", {"position": v(-44.78, -255.66) * mm});
            skCircle(sketch, "E115", {"center": v(-49.03, -257.15) * mm, "radius": 1.78 * mm});
            skPoint(sketch, "E115.first.point", {"position": v(-48.54, -258.86) * mm});
            skPoint(sketch, "E115.second.point", {"position": v(-48.9, -255.38) * mm});
            skPoint(sketch, "E115.third.point", {"position": v(-50.32, -255.93) * mm});
            skCircle(sketch, "E116", {"center": v(-62.86, -257.15) * mm, "radius": 1.78 * mm});
            skPoint(sketch, "E116.first.point", {"position": v(-63.19, -258.9) * mm});
            skPoint(sketch, "E116.second.point", {"position": v(-61.19, -256.55) * mm});
            skPoint(sketch, "E116.third.point", {"position": v(-63.14, -255.4) * mm});
            skCircle(sketch, "E117", {"center": v(-68.08, -257.15) * mm, "radius": 1.78 * mm});
            skPoint(sketch, "E117.first.point", {"position": v(-68.05, -258.93) * mm});
            skPoint(sketch, "E117.second.point", {"position": v(-67.31, -255.55) * mm});
            skPoint(sketch, "E117.third.point", {"position": v(-67.96, -255.38) * mm});
            skCircle(sketch, "E118", {"center": v(-65.47, -264.07) * mm, "radius": 2.03 * mm});
            skPoint(sketch, "E118.first.point", {"position": v(-64.11, -262.56) * mm});
            skPoint(sketch, "E118.second.point", {"position": v(-63.99, -265.45) * mm});
            skPoint(sketch, "E118.third.point", {"position": v(-67.23, -263.04) * mm});
            skCircle(sketch, "E119", {"center": v(-55.95, -264.07) * mm, "radius": 6.36 * mm});
            skPoint(sketch, "E119.first.point", {"position": v(-57.16, -270.31) * mm});
            skPoint(sketch, "E119.second.point", {"position": v(-50.22, -261.29) * mm});
            skPoint(sketch, "E119.third.point", {"position": v(-59.97, -259.14) * mm});
            skCircle(sketch, "E120", {"center": v(-46.42, -264.07) * mm, "radius": 2.03 * mm});
            skPoint(sketch, "E120.first.point", {"position": v(-46.28, -266.1) * mm});
            skPoint(sketch, "E120.second.point", {"position": v(-44.8, -262.85) * mm});
            skPoint(sketch, "E120.third.point", {"position": v(-46.82, -262.08) * mm});
            skCircle(sketch, "E121", {"center": v(-43.81, -270.98) * mm, "radius": 1.78 * mm});
            skPoint(sketch, "E121.first.point", {"position": v(-43.69, -272.76) * mm});
            skPoint(sketch, "E121.second.point", {"position": v(-42.27, -270.1) * mm});
            skPoint(sketch, "E121.third.point", {"position": v(-45, -269.66) * mm});
            skCircle(sketch, "E122", {"center": v(-49.03, -270.98) * mm, "radius": 1.78 * mm});
            skPoint(sketch, "E122.first.point", {"position": v(-49.14, -272.76) * mm});
            skPoint(sketch, "E122.second.point", {"position": v(-48.12, -269.45) * mm});
            skPoint(sketch, "E122.third.point", {"position": v(-49.9, -269.44) * mm});
            skCircle(sketch, "E123", {"center": v(-42.48, -277.54) * mm, "radius": 1.78 * mm});
            skPoint(sketch, "E123.first.point", {"position": v(-43.69, -278.84) * mm});
            skPoint(sketch, "E123.second.point", {"position": v(-41.43, -276.1) * mm});
            skPoint(sketch, "E123.third.point", {"position": v(-41.36, -278.92) * mm});
            skCircle(sketch, "E124", {"center": v(-69.42, -277.54) * mm, "radius": 1.78 * mm});
            skPoint(sketch, "E124.first.point", {"position": v(-70, -279.22) * mm});
            skPoint(sketch, "E124.second.point", {"position": v(-68.03, -276.42) * mm});
            skPoint(sketch, "E124.third.point", {"position": v(-70.7, -276.3) * mm});
            skCircle(sketch, "E125", {"center": v(-68.08, -270.98) * mm, "radius": 1.78 * mm});
            skPoint(sketch, "E125.first.point", {"position": v(-68.48, -272.71) * mm});
            skPoint(sketch, "E125.second.point", {"position": v(-66.85, -269.7) * mm});
            skPoint(sketch, "E125.third.point", {"position": v(-68.56, -269.27) * mm});
            skCircle(sketch, "E126", {"center": v(-62.86, -270.98) * mm, "radius": 1.78 * mm});
            skPoint(sketch, "E126.first.point", {"position": v(-63.29, -272.7) * mm});
            skPoint(sketch, "E126.second.point", {"position": v(-62.1, -269.37) * mm});
            skPoint(sketch, "E126.third.point", {"position": v(-64.02, -269.63) * mm});
            skCircle(sketch, "E127", {"center": v(127.08, -253.88) * mm, "radius": 1.78 * mm});
            skPoint(sketch, "E127.first.point", {"position": v(127.13, -252.1) * mm});
            skPoint(sketch, "E127.second.point", {"position": v(127.3, -255.65) * mm});
            skPoint(sketch, "E127.third.point", {"position": v(125.3, -253.92) * mm});
            skCircle(sketch, "E128", {"center": v(127.08, -273.44) * mm, "radius": 1.78 * mm});
            skPoint(sketch, "E128.first.point", {"position": v(127.24, -275.21) * mm});
            skPoint(sketch, "E128.second.point", {"position": v(128.28, -272.13) * mm});
            skPoint(sketch, "E128.third.point", {"position": v(126.4, -271.8) * mm});
            skPoint(sketch, "E129.first.point", {"position": v(120.92, -278.81) * mm});
            skPoint(sketch, "E129.second.point", {"position": v(122.74, -275.86) * mm});
            skPoint(sketch, "E129.third.point", {"position": v(119.95, -276.25) * mm});
            skPoint(sketch, "E130.first.point", {"position": v(133.9, -278.4) * mm});
            skPoint(sketch, "E130.second.point", {"position": v(132.72, -275.35) * mm});
            skPoint(sketch, "E130.third.point", {"position": v(131.11, -278.01) * mm});
            skPoint(sketch, "E131.first.point", {"position": v(132.91, -251.95) * mm});
            skPoint(sketch, "E131.second.point", {"position": v(132.88, -248.43) * mm});
            skPoint(sketch, "E131.third.point", {"position": v(130.92, -250.55) * mm});
            skPoint(sketch, "E132.first.point", {"position": v(119.82, -250.77) * mm});
            skPoint(sketch, "E132.second.point", {"position": v(122.8, -248.99) * mm});
            skPoint(sketch, "E132.third.point", {"position": v(120.62, -248.65) * mm});
            skCircle(sketch, "E133", {"center": v(113.6, -250.2) * mm, "radius": 1.78 * mm});
            skPoint(sketch, "E133.first.point", {"position": v(113.68, -248.41) * mm});
            skPoint(sketch, "E133.second.point", {"position": v(114.54, -251.7) * mm});
            skPoint(sketch, "E133.third.point", {"position": v(112.1, -251.12) * mm});
            skCircle(sketch, "E134", {"center": v(140.55, -250.2) * mm, "radius": 1.78 * mm});
            skPoint(sketch, "E134.first.point", {"position": v(141.05, -251.9) * mm});
            skPoint(sketch, "E134.second.point", {"position": v(140.75, -248.42) * mm});
            skPoint(sketch, "E134.third.point", {"position": v(138.79, -250.42) * mm});
            skCircle(sketch, "E135", {"center": v(139.21, -256.75) * mm, "radius": 1.78 * mm});
            skPoint(sketch, "E135.first.point", {"position": v(139.5, -255) * mm});
            skPoint(sketch, "E135.second.point", {"position": v(139.25, -258.52) * mm});
            skPoint(sketch, "E135.third.point", {"position": v(138.24, -255.26) * mm});
            skCircle(sketch, "E136", {"center": v(134, -256.75) * mm, "radius": 1.78 * mm});
            skPoint(sketch, "E136.first.point", {"position": v(134.48, -258.46) * mm});
            skPoint(sketch, "E136.second.point", {"position": v(134.13, -254.97) * mm});
            skPoint(sketch, "E136.third.point", {"position": v(132.7, -255.53) * mm});
            skCircle(sketch, "E137", {"center": v(120.16, -256.75) * mm, "radius": 1.78 * mm});
            skPoint(sketch, "E137.first.point", {"position": v(119.84, -258.5) * mm});
            skPoint(sketch, "E137.second.point", {"position": v(121.84, -256.14) * mm});
            skPoint(sketch, "E137.third.point", {"position": v(119.88, -255) * mm});
            skCircle(sketch, "E138", {"center": v(114.94, -256.75) * mm, "radius": 1.78 * mm});
            skPoint(sketch, "E138.first.point", {"position": v(114.98, -258.52) * mm});
            skPoint(sketch, "E138.second.point", {"position": v(115.71, -255.14) * mm});
            skPoint(sketch, "E138.third.point", {"position": v(115.06, -254.97) * mm});
            skCircle(sketch, "E139", {"center": v(117.55, -263.66) * mm, "radius": 2.03 * mm});
            skPoint(sketch, "E139.first.point", {"position": v(118.91, -262.15) * mm});
            skPoint(sketch, "E139.second.point", {"position": v(119.04, -265.05) * mm});
            skPoint(sketch, "E139.third.point", {"position": v(115.8, -262.64) * mm});
            skCircle(sketch, "E140", {"center": v(127.08, -263.66) * mm, "radius": 6.36 * mm});
            skPoint(sketch, "E140.first.point", {"position": v(125.86, -269.9) * mm});
            skPoint(sketch, "E140.second.point", {"position": v(132.8, -260.88) * mm});
            skPoint(sketch, "E140.third.point", {"position": v(123.06, -258.73) * mm});
            skCircle(sketch, "E141", {"center": v(136.6, -263.66) * mm, "radius": 2.03 * mm});
            skPoint(sketch, "E141.first.point", {"position": v(136.75, -265.69) * mm});
            skPoint(sketch, "E141.second.point", {"position": v(138.23, -262.44) * mm});
            skPoint(sketch, "E141.third.point", {"position": v(136.2, -261.67) * mm});
            skCircle(sketch, "E142", {"center": v(139.21, -270.58) * mm, "radius": 1.78 * mm});
            skPoint(sketch, "E142.first.point", {"position": v(139.34, -272.35) * mm});
            skPoint(sketch, "E142.second.point", {"position": v(140.76, -269.7) * mm});
            skPoint(sketch, "E142.third.point", {"position": v(138.02, -269.26) * mm});
            skCircle(sketch, "E143", {"center": v(134, -270.58) * mm, "radius": 1.78 * mm});
            skPoint(sketch, "E143.first.point", {"position": v(133.88, -272.35) * mm});
            skPoint(sketch, "E143.second.point", {"position": v(134.9, -269.05) * mm});
            skPoint(sketch, "E143.third.point", {"position": v(133.12, -269.03) * mm});
            skCircle(sketch, "E144", {"center": v(140.55, -277.13) * mm, "radius": 1.78 * mm});
            skPoint(sketch, "E144.first.point", {"position": v(139.34, -278.43) * mm});
            skPoint(sketch, "E144.second.point", {"position": v(141.6, -275.7) * mm});
            skPoint(sketch, "E144.third.point", {"position": v(141.66, -278.52) * mm});
            skCircle(sketch, "E145", {"center": v(113.6, -277.13) * mm, "radius": 1.78 * mm});
            skPoint(sketch, "E145.first.point", {"position": v(113.03, -278.81) * mm});
            skPoint(sketch, "E145.second.point", {"position": v(115, -276.01) * mm});
            skPoint(sketch, "E145.third.point", {"position": v(112.33, -275.9) * mm});
            skCircle(sketch, "E146", {"center": v(114.94, -270.58) * mm, "radius": 1.78 * mm});
            skPoint(sketch, "E146.first.point", {"position": v(114.54, -272.3) * mm});
            skPoint(sketch, "E146.second.point", {"position": v(116.17, -269.29) * mm});
            skPoint(sketch, "E146.third.point", {"position": v(114.46, -268.86) * mm});
            skCircle(sketch, "E147", {"center": v(120.16, -270.58) * mm, "radius": 1.78 * mm});
            skPoint(sketch, "E147.first.point", {"position": v(119.74, -272.3) * mm});
            skPoint(sketch, "E147.second.point", {"position": v(120.92, -268.97) * mm});
            skPoint(sketch, "E147.third.point", {"position": v(119, -269.23) * mm});
            skCircle(sketch, "E148", {"center": v(121.12, -44.81) * mm, "radius": 1.78 * mm});
            skPoint(sketch, "E148.first.point", {"position": v(121.18, -43.04) * mm});
            skPoint(sketch, "E148.second.point", {"position": v(121.35, -46.58) * mm});
            skPoint(sketch, "E148.third.point", {"position": v(119.35, -44.85) * mm});
            skCircle(sketch, "E149", {"center": v(121.12, -64.37) * mm, "radius": 1.78 * mm});
            skPoint(sketch, "E149.first.point", {"position": v(121.28, -66.14) * mm});
            skPoint(sketch, "E149.second.point", {"position": v(122.33, -63.06) * mm});
            skPoint(sketch, "E149.third.point", {"position": v(120.44, -62.73) * mm});
            skPoint(sketch, "E150.first.point", {"position": v(114.97, -69.74) * mm});
            skPoint(sketch, "E150.second.point", {"position": v(116.8, -66.8) * mm});
            skPoint(sketch, "E150.third.point", {"position": v(114, -67.18) * mm});
            skPoint(sketch, "E151.first.point", {"position": v(127.94, -69.34) * mm});
            skPoint(sketch, "E151.second.point", {"position": v(126.76, -66.29) * mm});
            skPoint(sketch, "E151.third.point", {"position": v(125.16, -68.94) * mm});
            skPoint(sketch, "E152.first.point", {"position": v(126.96, -42.88) * mm});
            skPoint(sketch, "E152.second.point", {"position": v(126.92, -39.36) * mm});
            skPoint(sketch, "E152.third.point", {"position": v(124.96, -41.48) * mm});
            skPoint(sketch, "E153.first.point", {"position": v(113.86, -41.7) * mm});
            skPoint(sketch, "E153.second.point", {"position": v(116.85, -39.92) * mm});
            skPoint(sketch, "E153.third.point", {"position": v(114.66, -39.58) * mm});
            skCircle(sketch, "E154", {"center": v(107.65, -41.12) * mm, "radius": 1.78 * mm});
            skPoint(sketch, "E154.first.point", {"position": v(107.73, -39.35) * mm});
            skPoint(sketch, "E154.second.point", {"position": v(108.59, -42.64) * mm});
            skPoint(sketch, "E154.third.point", {"position": v(106.14, -42.06) * mm});
            skCircle(sketch, "E155", {"center": v(134.6, -41.12) * mm, "radius": 1.78 * mm});
            skPoint(sketch, "E155.first.point", {"position": v(135.1, -42.83) * mm});
            skPoint(sketch, "E155.second.point", {"position": v(134.8, -39.36) * mm});
            skPoint(sketch, "E155.third.point", {"position": v(132.83, -41.35) * mm});
            skCircle(sketch, "E156", {"center": v(133.26, -47.68) * mm, "radius": 1.78 * mm});
            skPoint(sketch, "E156.first.point", {"position": v(133.54, -45.92) * mm});
            skPoint(sketch, "E156.second.point", {"position": v(133.3, -49.46) * mm});
            skPoint(sketch, "E156.third.point", {"position": v(132.29, -46.19) * mm});
            skCircle(sketch, "E157", {"center": v(128.04, -47.68) * mm, "radius": 1.78 * mm});
            skPoint(sketch, "E157.first.point", {"position": v(128.53, -49.39) * mm});
            skPoint(sketch, "E157.second.point", {"position": v(128.18, -45.9) * mm});
            skPoint(sketch, "E157.third.point", {"position": v(126.75, -46.46) * mm});
            skCircle(sketch, "E158", {"center": v(114.21, -47.68) * mm, "radius": 1.78 * mm});
            skPoint(sketch, "E158.first.point", {"position": v(113.89, -49.43) * mm});
            skPoint(sketch, "E158.second.point", {"position": v(115.88, -47.07) * mm});
            skPoint(sketch, "E158.third.point", {"position": v(113.93, -45.92) * mm});
            skCircle(sketch, "E159", {"center": v(108.99, -47.68) * mm, "radius": 1.78 * mm});
            skPoint(sketch, "E159.first.point", {"position": v(109.02, -49.45) * mm});
            skPoint(sketch, "E159.second.point", {"position": v(109.76, -46.08) * mm});
            skPoint(sketch, "E159.third.point", {"position": v(109.11, -45.9) * mm});
            skCircle(sketch, "E160", {"center": v(111.6, -54.6) * mm, "radius": 2.03 * mm});
            skPoint(sketch, "E160.first.point", {"position": v(112.96, -53.08) * mm});
            skPoint(sketch, "E160.second.point", {"position": v(113.09, -55.98) * mm});
            skPoint(sketch, "E160.third.point", {"position": v(109.84, -53.57) * mm});
            skCircle(sketch, "E161", {"center": v(121.12, -54.6) * mm, "radius": 6.36 * mm});
            skPoint(sketch, "E161.first.point", {"position": v(119.9, -60.84) * mm});
            skPoint(sketch, "E161.second.point", {"position": v(126.85, -51.81) * mm});
            skPoint(sketch, "E161.third.point", {"position": v(117.1, -49.66) * mm});
            skCircle(sketch, "E162", {"center": v(130.65, -54.6) * mm, "radius": 2.03 * mm});
            skPoint(sketch, "E162.first.point", {"position": v(130.8, -56.62) * mm});
            skPoint(sketch, "E162.second.point", {"position": v(132.28, -53.37) * mm});
            skPoint(sketch, "E162.third.point", {"position": v(130.25, -52.6) * mm});
            skCircle(sketch, "E163", {"center": v(133.26, -61.5) * mm, "radius": 1.78 * mm});
            skPoint(sketch, "E163.first.point", {"position": v(133.38, -63.28) * mm});
            skPoint(sketch, "E163.second.point", {"position": v(134.8, -60.62) * mm});
            skPoint(sketch, "E163.third.point", {"position": v(132.07, -60.19) * mm});
            skCircle(sketch, "E164", {"center": v(128.04, -61.5) * mm, "radius": 1.78 * mm});
            skPoint(sketch, "E164.first.point", {"position": v(127.93, -63.28) * mm});
            skPoint(sketch, "E164.second.point", {"position": v(128.95, -59.98) * mm});
            skPoint(sketch, "E164.third.point", {"position": v(127.16, -59.96) * mm});
            skCircle(sketch, "E165", {"center": v(134.6, -68.06) * mm, "radius": 1.78 * mm});
            skPoint(sketch, "E165.first.point", {"position": v(133.38, -69.36) * mm});
            skPoint(sketch, "E165.second.point", {"position": v(135.64, -66.62) * mm});
            skPoint(sketch, "E165.third.point", {"position": v(135.71, -69.45) * mm});
            skCircle(sketch, "E166", {"center": v(107.65, -68.06) * mm, "radius": 1.78 * mm});
            skPoint(sketch, "E166.first.point", {"position": v(107.08, -69.74) * mm});
            skPoint(sketch, "E166.second.point", {"position": v(109.04, -66.94) * mm});
            skPoint(sketch, "E166.third.point", {"position": v(106.38, -66.82) * mm});
            skCircle(sketch, "E167", {"center": v(108.99, -61.5) * mm, "radius": 1.78 * mm});
            skPoint(sketch, "E167.first.point", {"position": v(108.59, -63.24) * mm});
            skPoint(sketch, "E167.second.point", {"position": v(110.22, -60.22) * mm});
            skPoint(sketch, "E167.third.point", {"position": v(108.5, -59.8) * mm});
            skCircle(sketch, "E168", {"center": v(114.21, -61.5) * mm, "radius": 1.78 * mm});
            skPoint(sketch, "E168.first.point", {"position": v(113.78, -63.23) * mm});
            skPoint(sketch, "E168.second.point", {"position": v(114.97, -59.9) * mm});
            skPoint(sketch, "E168.third.point", {"position": v(113.05, -60.16) * mm});
            skCircle(sketch, "E169", {"center": v(-67.73, -73.68) * mm, "radius": 63.5 * mm});
            skSolve(sketch);
        }
        {
            var Q0;
            Q0=makeQuery(id+"F0.imprint","IMPRINT",FACE,{"disambiguationData":[TD([[makeQuery(id+"F0.imprint","IMPRINT",EDGE,{"derivedFrom":sQuery(id+"F0.wireOp",EDGE,"E0.bottom")}),1.0]])]});
            extrude(context, id + "F1", {"entities" : qUnion([Q0]), "depth" : 5.6 * mm, "offsetDistance" : 25.4 * mm});
        }
    });
